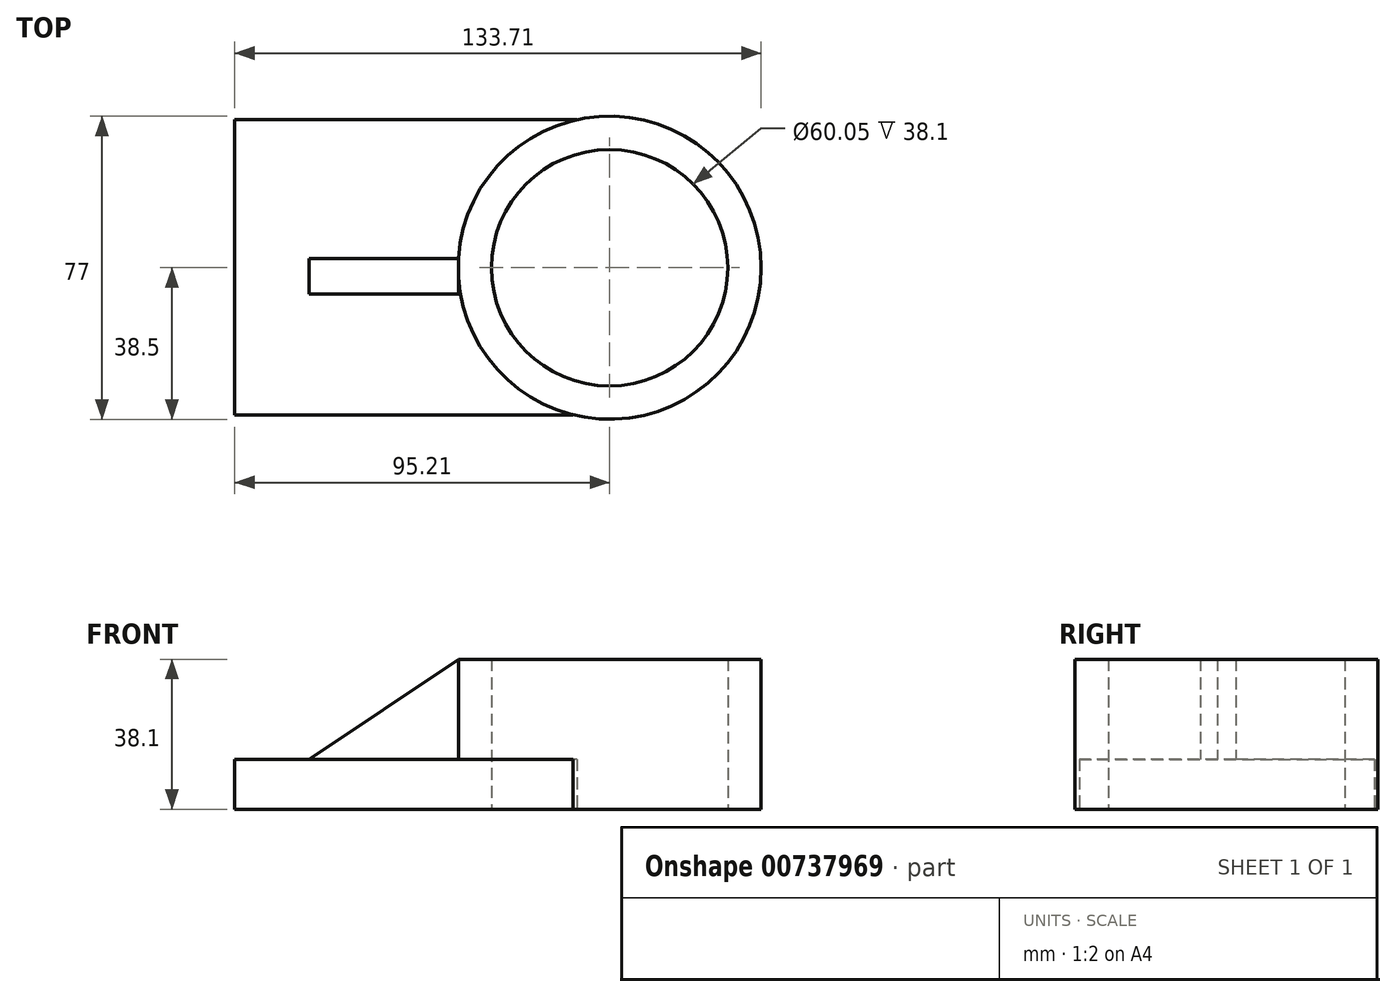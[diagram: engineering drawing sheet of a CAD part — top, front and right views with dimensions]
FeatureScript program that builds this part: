
annotation { "Feature Type Name" : "Feature", "Feature Type Description" : "" }
export const myFeature = defineFeature(function(context is Context, id is Id, definition is map)
    precondition{}
    {
        {
            var Q0;
            Q0=qCreatedBy(makeId("Top.planeOp"),FACE);
            var sketch = newSketch(context, id + "F0", { "sketchPlane" : qUnion([Q0])});
            skCircle(sketch, "E0", {"center": v(0, 0) * mm, "radius": 38.5 * mm});
            skCircle(sketch, "E1", {"center": v(0, 0) * mm, "radius": 30.02 * mm});
            skLineSegment(sketch, "E2.bottom", {"start": v(-12.43, 36.44) * mm, "end": v(-69.6, 36.44) * mm});
            skLineSegment(sketch, "E2.top", {"start": v(-12.43, -37.27) * mm, "end": v(-69.6, -37.27) * mm});
            skLineSegment(sketch, "E2.left", {"start": v(-12.43, 36.44) * mm, "end": v(-12.43, -37.27) * mm});
            skLineSegment(sketch, "E2.right", {"start": v(-69.6, 36.44) * mm, "end": v(-69.6, -37.27) * mm});
            skSolve(sketch);
        }
        {
            var Q0;
            {var subQ0=sQuery(id+"F0.wireOp",EDGE,"E2.left");var subQ4=sQuery(id+"F0.wireOp",EDGE,"E1");var subQ5=makeQuery(id+"F0.imprint","INTERSECT",VERTEX,{"disambiguationData":[OD(0.0)],"derivedFrom":[subQ4,subQ0]});Q0=makeQuery(id+"F0.imprint","IMPRINT",FACE,{"disambiguationData":[TD([[makeQuery(id+"F0.imprint","IMPRINT",EDGE,{"disambiguationData":[TD([[subQ5,1.0]])],"derivedFrom":subQ4}),-1.0]])]});}
            var Q1;
            {var subQ0=sQuery(id+"F0.wireOp",EDGE,"E2.left");var subQ4=sQuery(id+"F0.wireOp",EDGE,"E1");var subQ5=makeQuery(id+"F0.imprint","INTERSECT",VERTEX,{"disambiguationData":[OD(0.0)],"derivedFrom":[subQ4,subQ0]});Q1=makeQuery(id+"F0.imprint","IMPRINT",FACE,{"disambiguationData":[TD([[makeQuery(id+"F0.imprint","IMPRINT",EDGE,{"disambiguationData":[TD([[subQ5,-1.0]])],"derivedFrom":subQ4}),-1.0]])]});}
            extrude(context, id + "F1", {"entities" : qUnion([Q0, Q1]), "depth" : 38.1 * mm, "offsetDistance" : 25.4 * mm});
        }
        {
            var Q0;
            Q0=qCreatedBy(makeId("Top.planeOp"),FACE);
            var sketch = newSketch(context, id + "F2", { "sketchPlane" : qUnion([Q0])});
            skArc(sketch, "E3", {"start": v(-8.23, 37.37) * mm, "mid": v(-38.27, 0) * mm, "end": v(-8.23, -37.37) * mm});
            skLineSegment(sketch, "E4.bottom", {"start": v(-8.23, -37.37) * mm, "end": v(-95.21, -37.37) * mm});
            skLineSegment(sketch, "E4.top", {"start": v(-8.23, 37.65) * mm, "end": v(-95.21, 37.65) * mm});
            skLineSegment(sketch, "E4.left", {"start": v(-8.23, 37.37) * mm, "end": v(-8.23, 37.65) * mm});
            skLineSegment(sketch, "E4.right", {"start": v(-95.21, -37.37) * mm, "end": v(-95.21, 37.65) * mm});
            skSolve(sketch);
        }
        {
            var Q0;
            Q0 = qSketchRegion(id + "F2", true);
            extrude(context, id + "F3", {"entities" : qUnion([Q0]), "operationType" : NewBodyOperationType.ADD, "depth" : 12.7 * mm, "offsetDistance" : 25.4 * mm});
        }
        {
            var Q0;
            Q0=makeQuery(id+"F3.opExtrude","CAP_FACE",FACE,{"disambiguationData":[OSD([sQuery(id+"F2.wireOp",EDGE,"E3"),sQuery(id+"F2.wireOp",EDGE,"E4.bottom"),sQuery(id+"F2.wireOp",EDGE,"E4.top"),sQuery(id+"F2.wireOp",EDGE,"E4.left"),sQuery(id+"F2.wireOp",EDGE,"E4.right")])],"isStart":false});
            var sketch = newSketch(context, id + "F4", { "sketchPlane" : qUnion([Q0])});
            skLineSegment(sketch, "E5.bottom", {"start": v(-38.43, 2.37) * mm, "end": v(-76.32, 2.37) * mm});
            skLineSegment(sketch, "E5.top", {"start": v(-38.43, -6.62) * mm, "end": v(-76.32, -6.62) * mm});
            skLineSegment(sketch, "E5.left", {"start": v(-38.43, 2.37) * mm, "end": v(-38.43, -6.62) * mm});
            skLineSegment(sketch, "E5.right", {"start": v(-76.32, 2.37) * mm, "end": v(-76.32, -6.62) * mm});
            skSolve(sketch);
        }
        {
            var Q0;
            Q0 = qSketchRegion(id + "F4", true);
            extrude(context, id + "F5", {"entities" : qUnion([Q0]), "operationType" : NewBodyOperationType.ADD, "depth" : 25.4 * mm, "offsetDistance" : 25.4 * mm});
        }
        {
            var Q0;
            Q0=makeQuery(id+"F5.opExtrude","SWEPT_FACE",FACE,{"disambiguationData":[OSD([sQuery(id+"F4.wireOp",EDGE,"E5.bottom")])]});
            var sketch = newSketch(context, id + "F6", { "sketchPlane" : qUnion([Q0])});
            skLineSegment(sketch, "E6", {"start": v(38.43, 38.1) * mm, "end": v(76.32, 12.7) * mm});
            skSolve(sketch);
        }
        {
            var Q0;
            Q0=makeQuery(id+"F6.imprint","IMPRINT",FACE,{"disambiguationData":[TD([[makeQuery(id+"F6.imprint","IMPRINT",EDGE,{"derivedFrom":sQuery(id+"F6.wireOp",EDGE,"E6")}),1.0]])]});
            extrude(context, id + "F7", {"entities" : qUnion([Q0]), "operationType" : NewBodyOperationType.REMOVE, "oppositeDirection" : true, "depth" : 25.4 * mm, "offsetDistance" : 25.4 * mm});
        }
    });
